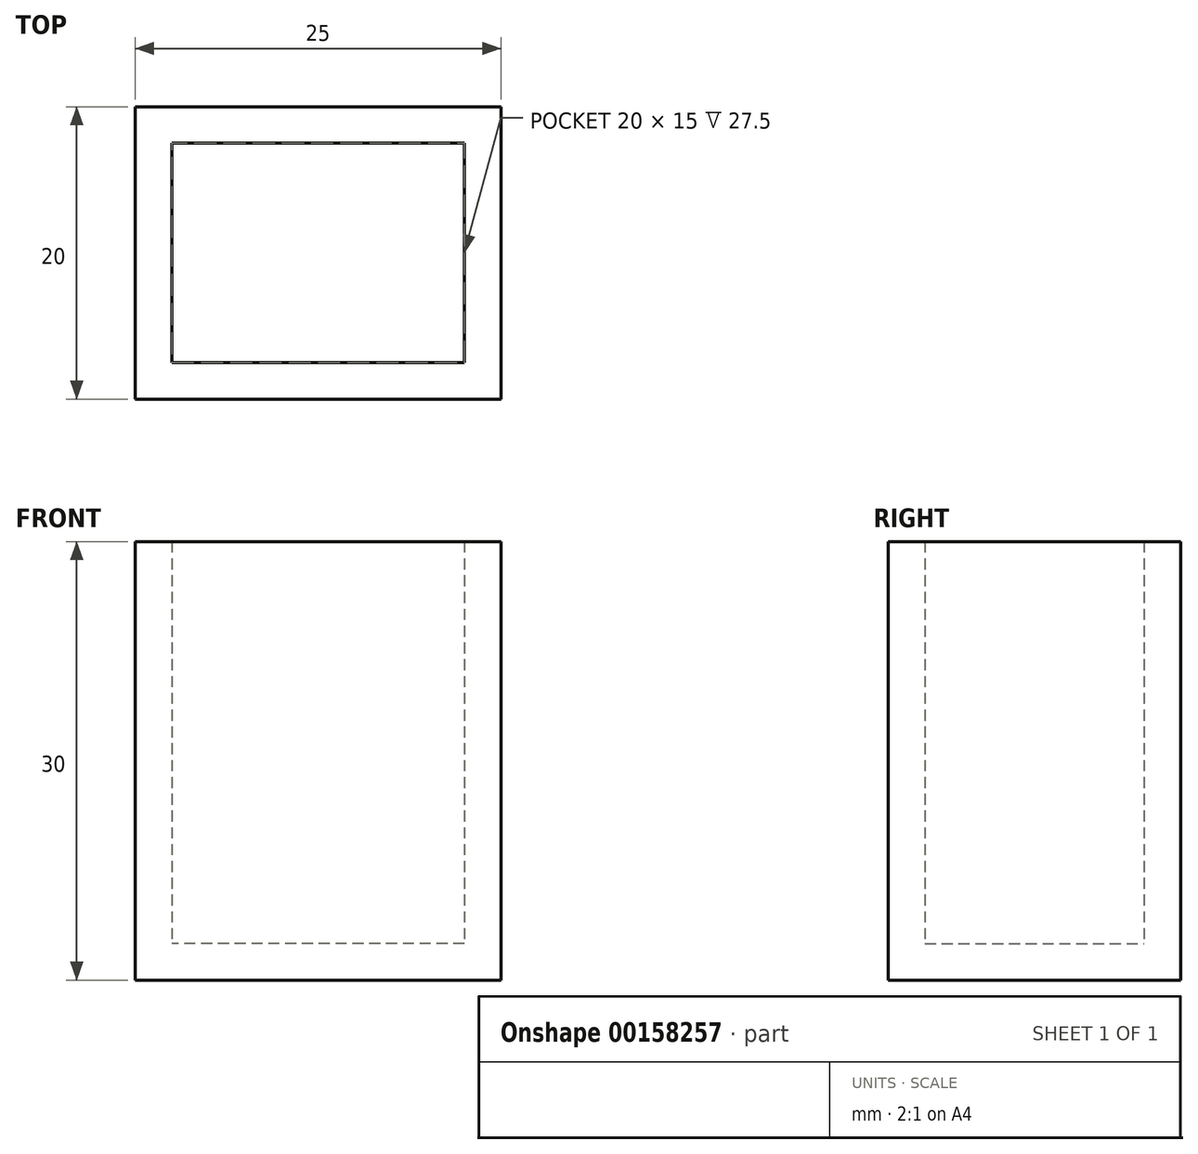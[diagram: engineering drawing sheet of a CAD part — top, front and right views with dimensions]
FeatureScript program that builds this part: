
annotation { "Feature Type Name" : "Feature", "Feature Type Description" : "" }
export const myFeature = defineFeature(function(context is Context, id is Id, definition is map)
    precondition{}
    {
        {
            var Q0;
            Q0=qCreatedBy(makeId("Right.planeOp"),FACE);
            var sketch = newSketch(context, id + "F0", { "sketchPlane" : qUnion([Q0])});
            skLineSegment(sketch, "E0.bottom", {"start": v(-45.3, 6.7) * mm, "end": v(-25.3, 6.7) * mm});
            skLineSegment(sketch, "E0.top", {"start": v(-45.3, -23.3) * mm, "end": v(-25.3, -23.3) * mm});
            skLineSegment(sketch, "E0.left", {"start": v(-45.3, 6.7) * mm, "end": v(-45.3, -23.3) * mm});
            skLineSegment(sketch, "E0.right", {"start": v(-25.3, 6.7) * mm, "end": v(-25.3, -23.3) * mm});
            skSolve(sketch);
        }
        {
            var Q0;
            Q0=makeQuery(id+"F0.imprint","IMPRINT",FACE,{"disambiguationData":[TD([[makeQuery(id+"F0.imprint","IMPRINT",EDGE,{"derivedFrom":sQuery(id+"F0.wireOp",EDGE,"E0.bottom")}),-1.0]])]});
            extrude(context, id + "F1", {"entities" : qUnion([Q0]), "depth" : 25 * mm});
        }
        {
            var Q0;
            Q0=makeQuery(id+"F1.opExtrude","SWEPT_FACE",FACE,{"disambiguationData":[OSD([sQuery(id+"F0.wireOp",EDGE,"E0.bottom")])]});
            shell(context, id + "F2", {"entities" : qUnion([Q0]), "thickness" : 2.5 * mm});
        }
    });
